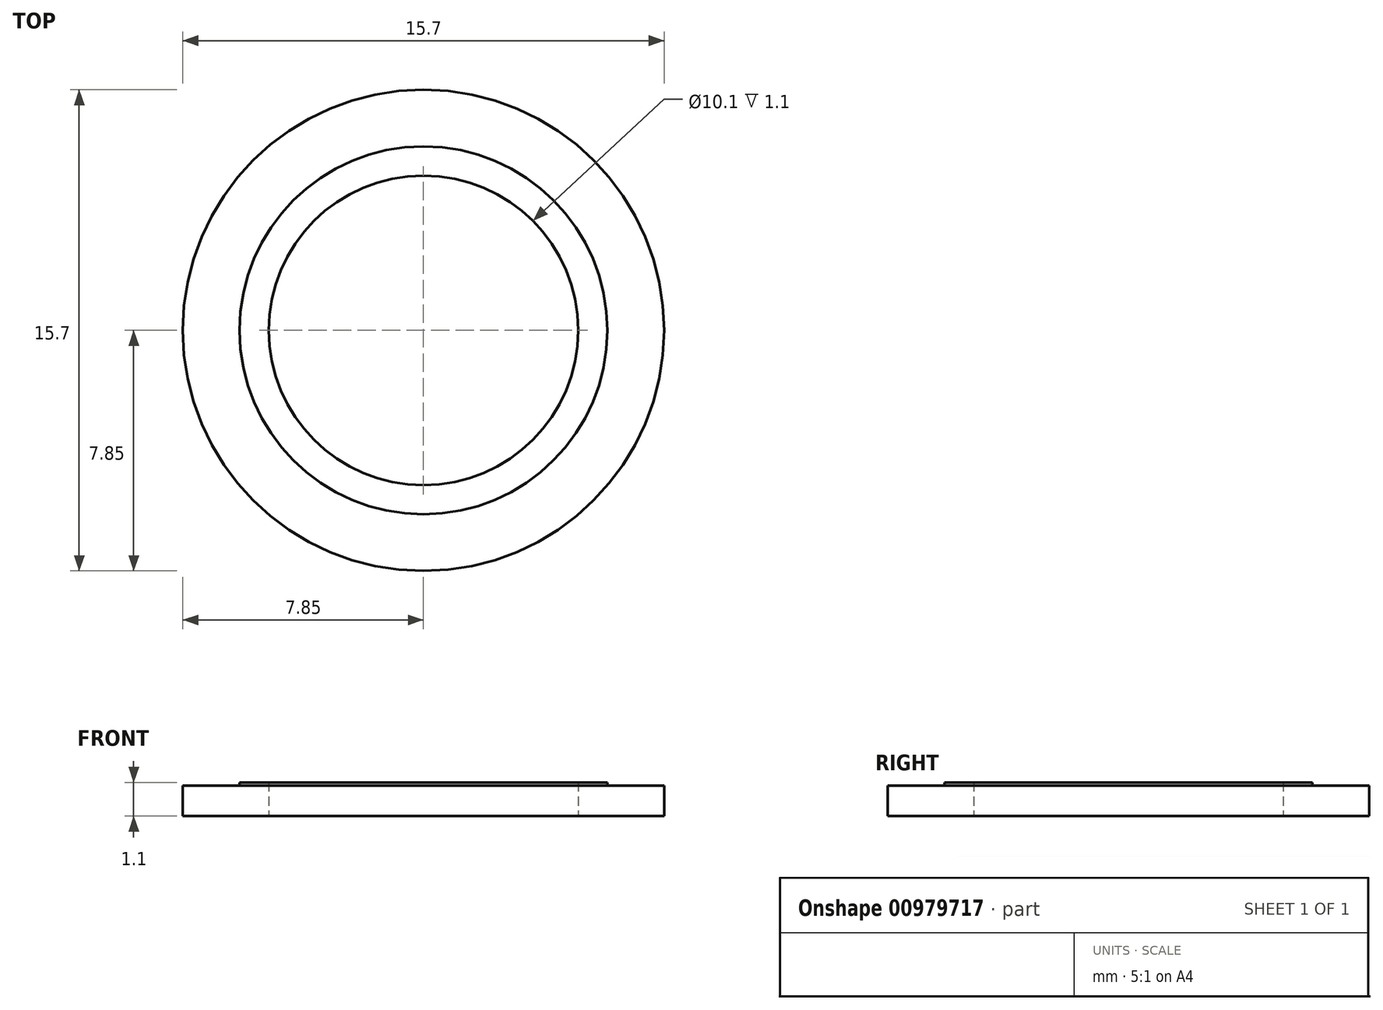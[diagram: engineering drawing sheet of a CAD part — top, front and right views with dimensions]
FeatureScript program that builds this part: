
annotation { "Feature Type Name" : "Feature", "Feature Type Description" : "" }
export const myFeature = defineFeature(function(context is Context, id is Id, definition is map)
    precondition{}
    {
        {
            var Q0;
            Q0=qCreatedBy(makeId("Front.planeOp"),FACE);
            var sketch = newSketch(context, id + "F0", { "sketchPlane" : qUnion([Q0])});
            skLineSegment(sketch, "E0.bottom", {"start": v(-5, 0) * mm, "end": v(-7.8, 0) * mm});
            skLineSegment(sketch, "E0.right", {"start": v(-7.8, 0) * mm, "end": v(-7.8, 1) * mm});
            skLineSegment(sketch, "E1.top", {"start": v(-5, 1.1) * mm, "end": v(-5.95, 1.1) * mm});
            skLineSegment(sketch, "E1.right", {"start": v(-5.95, 1) * mm, "end": v(-5.95, 1.1) * mm});
            skLineSegment(sketch, "E2", {"start": v(-7.8, 1) * mm, "end": v(-5.95, 1) * mm});
            skLineSegment(sketch, "E3", {"start": v(0.05, 1.1) * mm, "end": v(0.05, 2.38) * mm, "construction": true});
            skLineSegment(sketch, "E4", {"start": v(-5, 1.1) * mm, "end": v(-5, 0) * mm});
            skSolve(sketch);
        }
        {
            var Q0;
            Q0 = qSketchRegion(id + "F0", true);
            var Q1;
            Q1=sQuery(id+"F0.wireOp",EDGE,"E3");
            revolve(context, id + "F1", {"surfaceOperationType" : NewSurfaceOperationType.NEW, "entities" : qUnion([Q0]), "axis" : qUnion([Q1]), "revolveType" : RevolveType.FULL});
        }
    });
